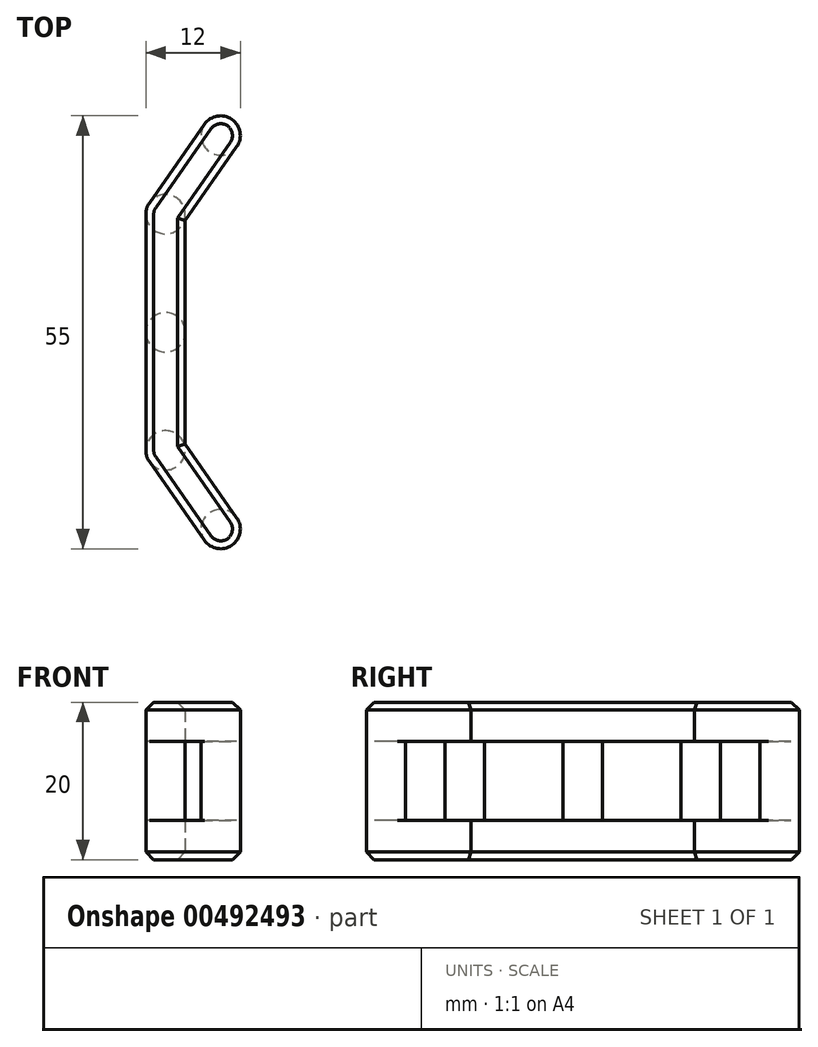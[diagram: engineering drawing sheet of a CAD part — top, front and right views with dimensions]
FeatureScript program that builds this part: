
annotation { "Feature Type Name" : "Feature", "Feature Type Description" : "" }
export const myFeature = defineFeature(function(context is Context, id is Id, definition is map)
    precondition{}
    {
        {
            var Q0;
            Q0=qCreatedBy(makeId("Top.planeOp"),FACE);
            var sketch = newSketch(context, id + "F0", { "sketchPlane" : qUnion([Q0])});
            skLineSegment(sketch, "E0.bottom", {"start": v(2.5, -15) * mm, "end": v(-2.5, -15) * mm, "construction": true});
            skLineSegment(sketch, "E0.top", {"start": v(2.5, 15) * mm, "end": v(-2.5, 15) * mm, "construction": true});
            skLineSegment(sketch, "E0.left", {"start": v(2.5, -15) * mm, "end": v(2.5, 15) * mm, "construction": true});
            skLineSegment(sketch, "E0.right", {"start": v(-2.5, -15) * mm, "end": v(-2.5, 15) * mm, "construction": true});
            skPoint(sketch, "E0.middle", {"position": v(0, 0) * mm});
            skCircle(sketch, "E1", {"center": v(0, 15) * mm, "radius": 2.5 * mm});
            skCircle(sketch, "E2", {"center": v(0, -15) * mm, "radius": 2.5 * mm});
            skLineSegment(sketch, "E3", {"start": v(0, 15) * mm, "end": v(0, 25) * mm, "construction": true});
            skLineSegment(sketch, "E4", {"start": v(0, 25) * mm, "end": v(7, 25) * mm, "construction": true});
            skLineSegment(sketch, "E5", {"start": v(0, -15) * mm, "end": v(0, -25) * mm, "construction": true});
            skLineSegment(sketch, "E6", {"start": v(0, -25) * mm, "end": v(7, -25) * mm, "construction": true});
            skCircle(sketch, "E7", {"center": v(7, -25) * mm, "radius": 2.5 * mm});
            skCircle(sketch, "E8", {"center": v(7, 25) * mm, "radius": 2.5 * mm});
            skLineSegment(sketch, "E9", {"start": v(9.05, 23.57) * mm, "end": v(2.05, 13.57) * mm});
            skLineSegment(sketch, "E10", {"start": v(-2.05, 16.43) * mm, "end": v(4.95, 26.43) * mm});
            skLineSegment(sketch, "E11", {"start": v(2.5, 15) * mm, "end": v(2.5, -15) * mm});
            skLineSegment(sketch, "E12", {"start": v(-2.5, -15) * mm, "end": v(-2.5, 15) * mm});
            skLineSegment(sketch, "E13", {"start": v(9.05, -23.57) * mm, "end": v(2.05, -13.57) * mm});
            skLineSegment(sketch, "E14", {"start": v(-2.05, -16.43) * mm, "end": v(4.95, -26.43) * mm});
            skSolve(sketch);
        }
        {
            var Q0;
            Q0 = qSketchRegion(id + "F0", true);
            extrude(context, id + "F1", {"entities" : qUnion([Q0]), "depth" : 5 * mm});
        }
        {
            var Q0;
            Q0=qCreatedBy(makeId("Top.planeOp"),FACE);
            var sketch = newSketch(context, id + "F2", { "sketchPlane" : qUnion([Q0])});
            skLineSegment(sketch, "E15", {"start": v(0, 0) * mm, "end": v(0, 15) * mm, "construction": true});
            skLineSegment(sketch, "E16", {"start": v(0, 0) * mm, "end": v(0, -15) * mm});
            skCircle(sketch, "E17", {"center": v(0, -15) * mm, "radius": 2.5 * mm});
            skCircle(sketch, "E18", {"center": v(0, 15) * mm, "radius": 2.5 * mm});
            skLineSegment(sketch, "E19", {"start": v(0, -15) * mm, "end": v(0, -25) * mm, "construction": true});
            skLineSegment(sketch, "E20", {"start": v(0, -25) * mm, "end": v(7, -25) * mm, "construction": true});
            skLineSegment(sketch, "E21", {"start": v(0, 15) * mm, "end": v(0, 25) * mm, "construction": true});
            skLineSegment(sketch, "E22", {"start": v(0, 25) * mm, "end": v(7, 25) * mm, "construction": true});
            skCircle(sketch, "E23", {"center": v(7, 25) * mm, "radius": 2.5 * mm});
            skCircle(sketch, "E24", {"center": v(7, -25) * mm, "radius": 2.5 * mm});
            skSolve(sketch);
        }
        {
            var Q0;
            Q0 = qSketchRegion(id + "F2", true);
            extrude(context, id + "F3", {"entities" : qUnion([Q0]), "operationType" : NewBodyOperationType.ADD, "depth" : 20 * mm});
        }
        {
            var Q0;
            Q0=qCreatedBy(makeId("Top.planeOp"),FACE);
            cPlane(context, id + "F4", {"entities" : qUnion([Q0]), "cplaneType" : CPlaneType.OFFSET, "offset" : 15 * mm, "width" : 150 * mm, "height" : 150 * mm});
        }
        {
            var Q0;
            Q0=qCreatedBy(id+"F4.planeOp",FACE);
            var sketch = newSketch(context, id + "F5", { "sketchPlane" : qUnion([Q0])});
            skLineSegment(sketch, "E25.bottom", {"start": v(2.5, -15) * mm, "end": v(-2.5, -15) * mm, "construction": true});
            skLineSegment(sketch, "E25.top", {"start": v(2.5, 15) * mm, "end": v(-2.5, 15) * mm, "construction": true});
            skLineSegment(sketch, "E25.left", {"start": v(2.5, -15) * mm, "end": v(2.5, 15) * mm, "construction": true});
            skLineSegment(sketch, "E25.right", {"start": v(-2.5, -15) * mm, "end": v(-2.5, 15) * mm, "construction": true});
            skPoint(sketch, "E25.middle", {"position": v(0, 0) * mm});
            skCircle(sketch, "E26", {"center": v(0, 15) * mm, "radius": 2.5 * mm});
            skCircle(sketch, "E27", {"center": v(0, -15) * mm, "radius": 2.5 * mm});
            skLineSegment(sketch, "E28", {"start": v(0, 15) * mm, "end": v(0, 25) * mm, "construction": true});
            skLineSegment(sketch, "E29", {"start": v(0, 25) * mm, "end": v(7, 25) * mm, "construction": true});
            skLineSegment(sketch, "E30", {"start": v(0, -15) * mm, "end": v(0, -25) * mm, "construction": true});
            skLineSegment(sketch, "E31", {"start": v(0, -25) * mm, "end": v(7, -25) * mm, "construction": true});
            skCircle(sketch, "E32", {"center": v(7, -25) * mm, "radius": 2.5 * mm});
            skCircle(sketch, "E33", {"center": v(7, 25) * mm, "radius": 2.5 * mm});
            skLineSegment(sketch, "E34", {"start": v(9.05, 23.57) * mm, "end": v(2.05, 13.57) * mm});
            skLineSegment(sketch, "E35", {"start": v(-2.05, 16.43) * mm, "end": v(4.95, 26.43) * mm});
            skLineSegment(sketch, "E36", {"start": v(2.5, 15) * mm, "end": v(2.5, -15) * mm});
            skLineSegment(sketch, "E37", {"start": v(-2.5, -15) * mm, "end": v(-2.5, 15) * mm});
            skLineSegment(sketch, "E38", {"start": v(9.05, -23.57) * mm, "end": v(2.05, -13.57) * mm});
            skLineSegment(sketch, "E39", {"start": v(-2.05, -16.43) * mm, "end": v(4.95, -26.43) * mm});
            skSolve(sketch);
        }
        {
            var Q0;
            Q0 = qSketchRegion(id + "F5", true);
            extrude(context, id + "F6", {"entities" : qUnion([Q0]), "operationType" : NewBodyOperationType.ADD, "depth" : 5 * mm});
        }
        {
            var Q0;
            Q0=qCreatedBy(id+"F4.planeOp",FACE);
            var sketch = newSketch(context, id + "F7", { "sketchPlane" : qUnion([Q0])});
            skCircle(sketch, "E40", {"center": v(0, 0) * mm, "radius": 2.5 * mm});
            skSolve(sketch);
        }
        {
            var Q0;
            Q0 = qSketchRegion(id + "F7", true);
            extrude(context, id + "F8", {"entities" : qUnion([Q0]), "operationType" : NewBodyOperationType.ADD, "oppositeDirection" : true, "depth" : 10 * mm});
        }
        {
            var Q0;
            Q0=makeQuery(id+"F1.opExtrude","CAP_EDGE",EDGE,{"disambiguationData":[OSD([sQuery(id+"F0.wireOp",EDGE,"E9")])],"isStart":true});
            var Q1;
            Q1=makeQuery(id+"F1.opExtrude","CAP_EDGE",EDGE,{"disambiguationData":[OSD([sQuery(id+"F0.wireOp",EDGE,"E11")])],"isStart":true});
            var Q2;
            Q2=makeQuery(id+"F6.boolean.opBoolean","MERGE",FACE,{"derivedFrom":[makeQuery(id+"F3.opExtrude","CAP_FACE",FACE,{"disambiguationData":[OSD([sQuery(id+"F2.wireOp",EDGE,"E17")])],"isStart":false}),makeQuery(id+"F3.opExtrude","CAP_FACE",FACE,{"disambiguationData":[OSD([sQuery(id+"F2.wireOp",EDGE,"E18")])],"isStart":false}),makeQuery(id+"F3.opExtrude","CAP_FACE",FACE,{"disambiguationData":[OSD([sQuery(id+"F2.wireOp",EDGE,"E23")])],"isStart":false}),makeQuery(id+"F3.opExtrude","CAP_FACE",FACE,{"disambiguationData":[OSD([sQuery(id+"F2.wireOp",EDGE,"E24")])],"isStart":false}),makeQuery(id+"F6.opExtrude","CAP_FACE",FACE,{"disambiguationData":[OSD([sQuery(id+"F5.wireOp",EDGE,"E26"),sQuery(id+"F5.wireOp",EDGE,"E27"),sQuery(id+"F5.wireOp",EDGE,"E32"),sQuery(id+"F5.wireOp",EDGE,"E33"),sQuery(id+"F5.wireOp",EDGE,"E34"),sQuery(id+"F5.wireOp",EDGE,"E35"),sQuery(id+"F5.wireOp",EDGE,"E36"),sQuery(id+"F5.wireOp",EDGE,"E37"),sQuery(id+"F5.wireOp",EDGE,"E38"),sQuery(id+"F5.wireOp",EDGE,"E39")])],"isStart":false})]});
            chamfer(context, id + "F9", {"entities" : qUnion([Q0, Q1, Q2]), "width" : 1 * mm, "tangentPropagation" : true});
        }
    });
